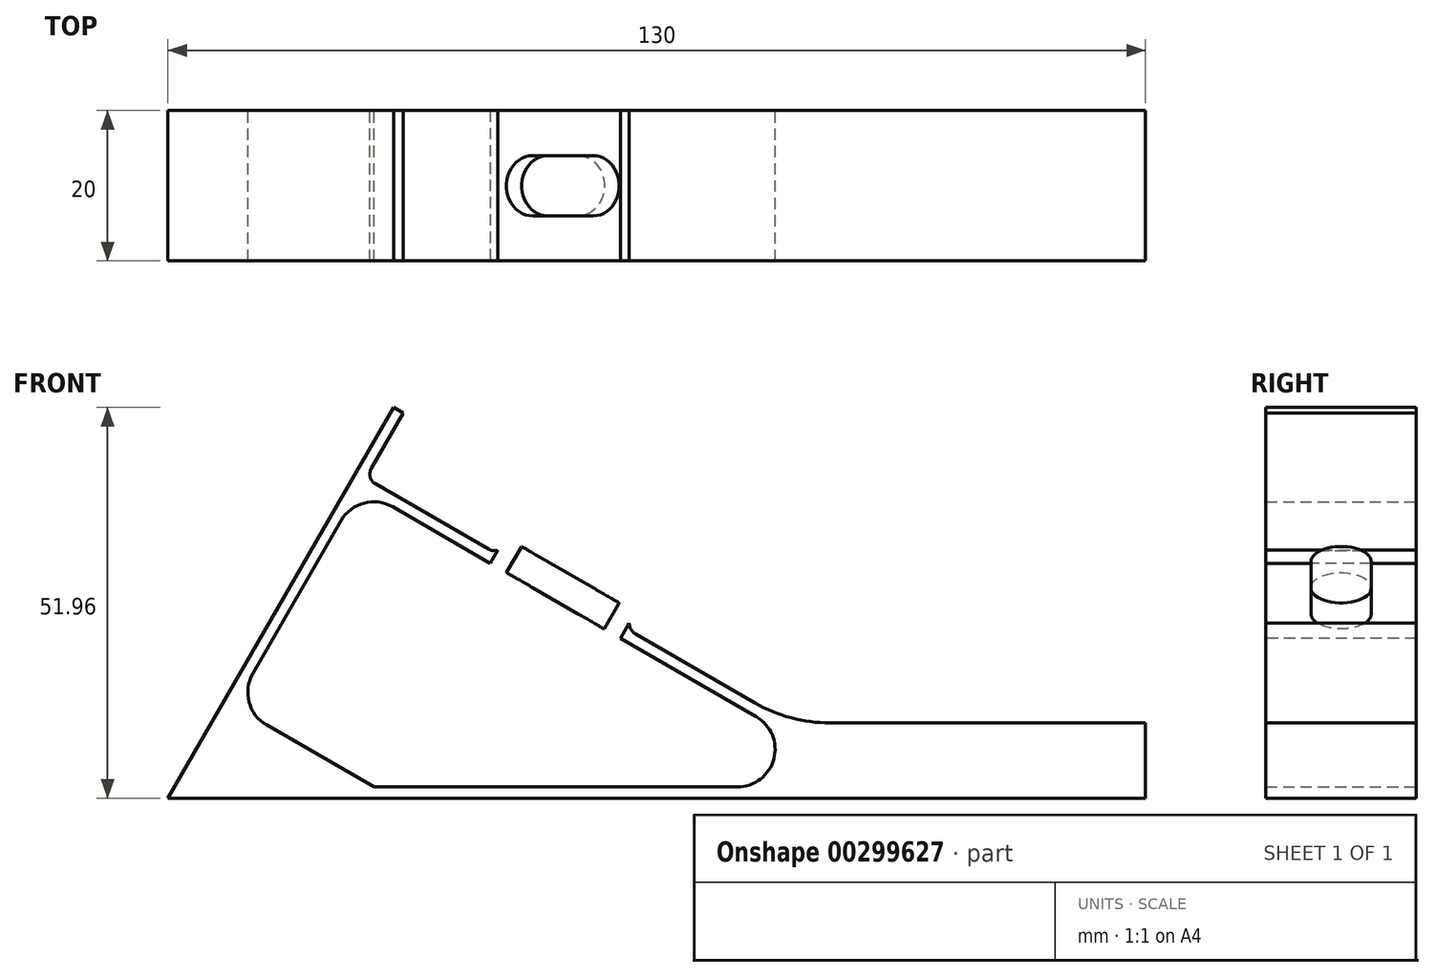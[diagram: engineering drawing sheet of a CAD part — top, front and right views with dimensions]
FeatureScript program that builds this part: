
annotation { "Feature Type Name" : "Feature", "Feature Type Description" : "" }
export const myFeature = defineFeature(function(context is Context, id is Id, definition is map)
    precondition{}
    {
        {
            var Q0;
            Q0=qCreatedBy(makeId("Front.planeOp"),FACE);
            var sketch = newSketch(context, id + "F0", { "sketchPlane" : qUnion([Q0])});
            skLineSegment(sketch, "E0", {"start": v(0, 0) * mm, "end": v(130, 0) * mm});
            skLineSegment(sketch, "E1", {"start": v(130, 0) * mm, "end": v(130, 10) * mm});
            skLineSegment(sketch, "E2", {"start": v(130, 10) * mm, "end": v(88.04, 10) * mm});
            skLineSegment(sketch, "E3", {"start": v(0, 0) * mm, "end": v(30, 51.96) * mm});
            skLineSegment(sketch, "E4", {"start": v(30, 51.96) * mm, "end": v(31.3, 51.21) * mm});
            skLineSegment(sketch, "E5", {"start": v(31.3, 51.21) * mm, "end": v(27.05, 43.85) * mm});
            skLineSegment(sketch, "E6", {"start": v(11.3, 16.57) * mm, "end": v(23.05, 36.92) * mm});
            skLineSegment(sketch, "E7", {"start": v(27.4, 1.5) * mm, "end": v(75.74, 1.5) * mm});
            skLineSegment(sketch, "E8", {"start": v(27.4, 1.5) * mm, "end": v(13.13, 9.74) * mm});
            skArc(sketch, "E9", {"start": v(11.3, 16.57) * mm, "mid": v(10.8, 12.78) * mm, "end": v(13.13, 9.74) * mm});
            skArc(sketch, "E10", {"start": v(75.74, 1.5) * mm, "mid": v(80.57, 5.2) * mm, "end": v(78.24, 10.83) * mm});
            skLineSegment(sketch, "E11", {"start": v(78.24, 10.83) * mm, "end": v(29.88, 38.75) * mm});
            skArc(sketch, "E12", {"start": v(29.88, 38.75) * mm, "mid": v(26.09, 39.25) * mm, "end": v(23.05, 36.92) * mm});
            skLineSegment(sketch, "E13", {"start": v(78.04, 12.68) * mm, "end": v(62.2, 21.83) * mm});
            skLineSegment(sketch, "E14", {"start": v(62.2, 24.72) * mm, "end": v(44.87, 34.72) * mm});
            skLineSegment(sketch, "E15", {"start": v(42.65, 33.11) * mm, "end": v(27.6, 41.8) * mm});
            skArc(sketch, "E16", {"start": v(27.05, 43.85) * mm, "mid": v(26.9, 42.71) * mm, "end": v(27.6, 41.8) * mm});
            skArc(sketch, "E17", {"start": v(78.04, 12.68) * mm, "mid": v(82.86, 10.68) * mm, "end": v(88.04, 10) * mm});
            skArc(sketch, "E18", {"start": v(62.2, 24.72) * mm, "mid": v(61.36, 23.27) * mm, "end": v(62.2, 21.83) * mm});
            skArc(sketch, "E19", {"start": v(42.65, 33.11) * mm, "mid": v(44.28, 33.2) * mm, "end": v(44.87, 34.72) * mm});
            skSolve(sketch);
        }
        {
            var Q0;
            Q0=makeQuery(id+"F0.imprint","IMPRINT",FACE,{"disambiguationData":[TD([[makeQuery(id+"F0.imprint","IMPRINT",EDGE,{"derivedFrom":sQuery(id+"F0.wireOp",EDGE,"E0")}),1.0]])]});
            extrude(context, id + "F1", {"entities" : qUnion([Q0]), "endBound" : BoundingType.SYMMETRIC, "depth" : 20 * mm});
        }
        {
            var Q0;
            Q0=makeQuery(id+"F1.opExtrude","SWEPT_FACE",FACE,{"disambiguationData":[OSD([sQuery(id+"F0.wireOp",EDGE,"E14")])]});
            var sketch = newSketch(context, id + "F2", { "sketchPlane" : qUnion([Q0])});
            skLineSegment(sketch, "E20", {"start": v(28, 0) * mm, "end": v(35, 0) * mm, "construction": true});
            skArc(sketch, "E21.0.startCap", {"start": v(28, -4) * mm, "mid": v(24, 0) * mm, "end": v(28, 4) * mm});
            skArc(sketch, "E21.0.endCap", {"start": v(35, 4) * mm, "mid": v(39, 0) * mm, "end": v(35, -4) * mm});
            skLineSegment(sketch, "E21.0.left", {"start": v(28, 4) * mm, "end": v(35, 4) * mm});
            skLineSegment(sketch, "E21.0.right", {"start": v(28, -4) * mm, "end": v(35, -4) * mm});
            skSolve(sketch);
        }
        {
            var Q0;
            Q0=makeQuery(id+"F2.imprint","IMPRINT",FACE,{"disambiguationData":[TD([[makeQuery(id+"F2.imprint","IMPRINT",EDGE,{"derivedFrom":sQuery(id+"F2.wireOp",EDGE,"E21.0.startCap")}),-1.0]])]});
            extrude(context, id + "F3", {"entities" : qUnion([Q0]), "operationType" : NewBodyOperationType.REMOVE, "oppositeDirection" : true, "depth" : 5 * mm});
        }
    });
